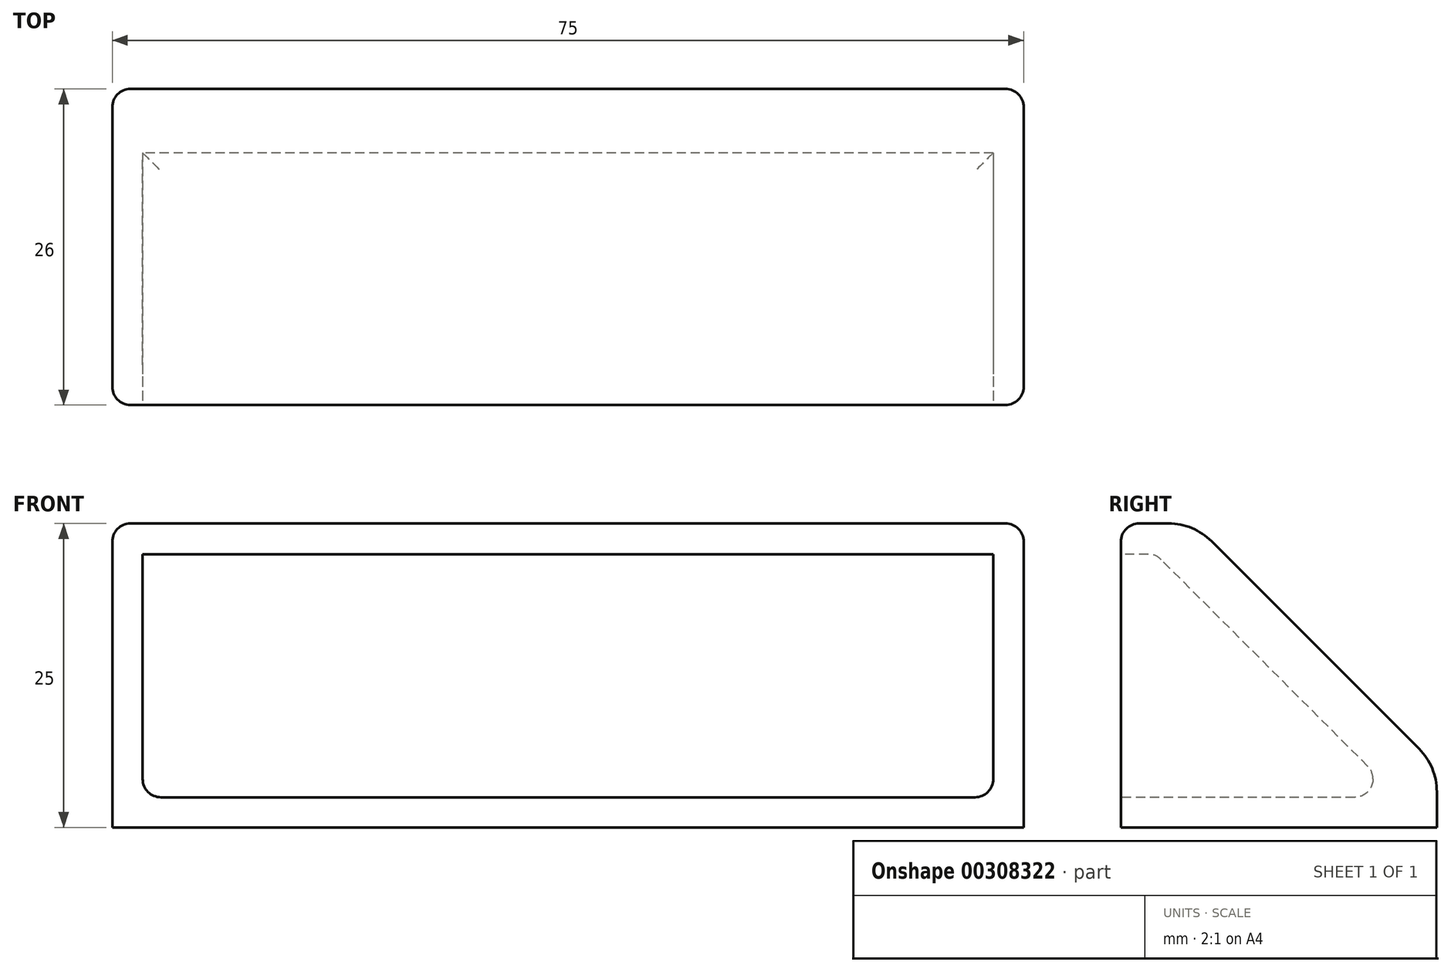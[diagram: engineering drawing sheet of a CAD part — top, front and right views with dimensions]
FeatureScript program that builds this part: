
annotation { "Feature Type Name" : "Feature", "Feature Type Description" : "" }
export const myFeature = defineFeature(function(context is Context, id is Id, definition is map)
    precondition{}
    {
        {
            var Q0;
            Q0=qCreatedBy(makeId("Top.planeOp"),FACE);
            var sketch = newSketch(context, id + "F0", { "sketchPlane" : qUnion([Q0])});
            skLineSegment(sketch, "E0.bottom", {"start": v(37.5, 13) * mm, "end": v(-37.5, 13) * mm});
            skLineSegment(sketch, "E0.top", {"start": v(37.5, -13) * mm, "end": v(-37.5, -13) * mm});
            skLineSegment(sketch, "E0.left", {"start": v(37.5, 13) * mm, "end": v(37.5, -13) * mm});
            skLineSegment(sketch, "E0.right", {"start": v(-37.5, 13) * mm, "end": v(-37.5, -13) * mm});
            skPoint(sketch, "E0.middle", {"position": v(0, 0) * mm});
            skSolve(sketch);
        }
        {
            var Q0;
            Q0=makeQuery(id+"F0.imprint","IMPRINT",FACE,{"disambiguationData":[TD([[makeQuery(id+"F0.imprint","IMPRINT",EDGE,{"derivedFrom":sQuery(id+"F0.wireOp",EDGE,"E0.bottom")}),1.0]])]});
            extrude(context, id + "F1", {"entities" : qUnion([Q0]), "depth" : 25 * mm});
        }
        {
            var Q0;
            Q0=makeQuery(id+"F1.opExtrude","CAP_EDGE",EDGE,{"disambiguationData":[OSD([sQuery(id+"F0.wireOp",EDGE,"E0.bottom")])],"isStart":false});
            chamfer(context, id + "F2", {"entities" : qUnion([Q0]), "width" : 20 * mm, "tangentPropagation" : true});
        }
        {
            var Q0;
            Q0=makeQuery(id+"F1.opExtrude","SWEPT_FACE",FACE,{"disambiguationData":[OSD([sQuery(id+"F0.wireOp",EDGE,"E0.top")])]});
            var sketch = newSketch(context, id + "F3", { "sketchPlane" : qUnion([Q0])});
            skLineSegment(sketch, "E1.bottom", {"start": v(-35, 2.48) * mm, "end": v(35, 2.48) * mm});
            skLineSegment(sketch, "E1.top", {"start": v(-35, 22.48) * mm, "end": v(35, 22.48) * mm});
            skLineSegment(sketch, "E1.left", {"start": v(-35, 2.48) * mm, "end": v(-35, 22.48) * mm});
            skLineSegment(sketch, "E1.right", {"start": v(35, 2.48) * mm, "end": v(35, 22.48) * mm});
            skSolve(sketch);
        }
        {
            var Q0;
            Q0 = qSketchRegion(id + "F3", true);
            extrude(context, id + "F4", {"entities" : qUnion([Q0]), "operationType" : NewBodyOperationType.REMOVE, "oppositeDirection" : true, "depth" : 23 * mm});
        }
        {
            var Q0;
            Q0=makeQuery(id+"F1.opExtrude","SWEPT_FACE",FACE,{"disambiguationData":[OSD([sQuery(id+"F0.wireOp",EDGE,"E0.right")])]});
            var sketch = newSketch(context, id + "F5", { "sketchPlane" : qUnion([Q0])});
            skLineSegment(sketch, "E2", {"start": v(-10.4, 7.6) * mm, "end": v(-10.4, 1.94) * mm});
            skLineSegment(sketch, "E3", {"start": v(-10.4, 1.94) * mm, "end": v(7.25, 19.6) * mm});
            skLineSegment(sketch, "E4", {"start": v(7.25, 19.6) * mm, "end": v(11.27, 23.61) * mm});
            skLineSegment(sketch, "E5", {"start": v(5.61, 23.61) * mm, "end": v(11.27, 23.61) * mm});
            skLineSegment(sketch, "E6", {"start": v(5.61, 23.61) * mm, "end": v(-10.4, 7.6) * mm});
            skSolve(sketch);
        }
        {
            var Q0;
            Q0 = qSketchRegion(id + "F5", true);
            var Q1;
            {var subQ0=sQuery(id+"F5.wireOp",EDGE,"khBEoFIl-ztzK-T5dB-HSFU-Ecbhnp3rjpfp");Q1=makeQuery(id+"F5.imprint","IMPRINT",FACE,{"disambiguationData":[TD([[makeQuery(id+"F5.imprint","IMPRINT",EDGE,{"derivedFrom":subQ0}),1.0]])]});}
            extrude(context, id + "F6", {"entities" : qUnion([Q0, Q1]), "operationType" : NewBodyOperationType.ADD, "oppositeDirection" : true, "depth" : 72.5 * mm});
        }
        {
            var Q0;
            Q0=makeQuery(id+"F1.opExtrude","SWEPT_EDGE",EDGE,{"disambiguationData":[OSD([sQuery(id+"F0.wireOp",EDGE,"E0.top"),sQuery(id+"F0.wireOp",EDGE,"E0.left")])]});
            var Q1;
            Q1=makeQuery(id+"F1.opExtrude","CAP_EDGE",EDGE,{"disambiguationData":[OSD([sQuery(id+"F0.wireOp",EDGE,"E0.top")])],"isStart":false});
            var Q2;
            Q2=makeQuery(id+"F4.boolean.opBoolean","COPY",EDGE,{"derivedFrom":makeQuery(id+"F4.opExtrude","CAP_EDGE",EDGE,{"disambiguationData":[OSD([sQuery(id+"F3.wireOp",EDGE,"E1.bottom")])],"isStart":true})});
            var Q3;
            Q3=makeQuery(id+"F4.boolean.opBoolean","COPY",EDGE,{"derivedFrom":makeQuery(id+"F4.opExtrude","CAP_EDGE",EDGE,{"disambiguationData":[OSD([sQuery(id+"F3.wireOp",EDGE,"E1.right")])],"isStart":true})});
            var Q4;
            Q4=makeQuery(id+"F4.boolean.opBoolean","COPY",EDGE,{"derivedFrom":makeQuery(id+"F4.opExtrude","CAP_EDGE",EDGE,{"disambiguationData":[OSD([sQuery(id+"F3.wireOp",EDGE,"E1.left")])],"isStart":true})});
            var Q5;
            Q5=makeQuery(id+"F4.boolean.opBoolean","COPY",EDGE,{"derivedFrom":makeQuery(id+"F4.opExtrude","CAP_EDGE",EDGE,{"disambiguationData":[OSD([sQuery(id+"F3.wireOp",EDGE,"E1.top")])],"isStart":true})});
            var Q6;
            Q6=makeQuery(id+"F1.opExtrude","SWEPT_EDGE",EDGE,{"disambiguationData":[OSD([sQuery(id+"F0.wireOp",EDGE,"E0.top"),sQuery(id+"F0.wireOp",EDGE,"E0.right")])]});
            var Q7;
            Q7=makeQuery(id+"F1.opExtrude","SWEPT_EDGE",EDGE,{"disambiguationData":[OSD([sQuery(id+"F0.wireOp",EDGE,"E0.bottom"),sQuery(id+"F0.wireOp",EDGE,"E0.left")])]});
            var Q8;
            Q8=makeQuery(id+"F2.opChamfer","BLEND_EDGE",EDGE,{"blendedFrom":[makeQuery(id+"F1.opExtrude","CAP_EDGE",EDGE,{"disambiguationData":[OSD([sQuery(id+"F0.wireOp",EDGE,"E0.bottom")])],"isStart":false}),makeQuery(id+"F1.opExtrude","SWEPT_FACE",FACE,{"disambiguationData":[OSD([sQuery(id+"F0.wireOp",EDGE,"E0.left")])]})],"blendedInto":[makeQuery(id+"F1.opExtrude","SWEPT_FACE",FACE,{"disambiguationData":[OSD([sQuery(id+"F0.wireOp",EDGE,"E0.left")])]})]});
            var Q9;
            Q9=makeQuery(id+"F1.opExtrude","CAP_EDGE",EDGE,{"disambiguationData":[OSD([sQuery(id+"F0.wireOp",EDGE,"E0.left")])],"isStart":false});
            var Q10;
            Q10=makeQuery(id+"F1.opExtrude","CAP_EDGE",EDGE,{"disambiguationData":[OSD([sQuery(id+"F0.wireOp",EDGE,"E0.right")])],"isStart":false});
            var Q11;
            Q11=makeQuery(id+"F2.opChamfer","BLEND_EDGE",EDGE,{"blendedFrom":[makeQuery(id+"F1.opExtrude","CAP_EDGE",EDGE,{"disambiguationData":[OSD([sQuery(id+"F0.wireOp",EDGE,"E0.bottom")])],"isStart":false}),makeQuery(id+"F1.opExtrude","SWEPT_FACE",FACE,{"disambiguationData":[OSD([sQuery(id+"F0.wireOp",EDGE,"E0.right")])]})],"blendedInto":[makeQuery(id+"F1.opExtrude","SWEPT_FACE",FACE,{"disambiguationData":[OSD([sQuery(id+"F0.wireOp",EDGE,"E0.right")])]})]});
            var Q12;
            Q12=makeQuery(id+"F1.opExtrude","SWEPT_EDGE",EDGE,{"disambiguationData":[OSD([sQuery(id+"F0.wireOp",EDGE,"E0.bottom"),sQuery(id+"F0.wireOp",EDGE,"E0.right")])]});
            var Q13;
            Q13=makeQuery(id+"F4.boolean.opBoolean","COPY",EDGE,{"derivedFrom":makeQuery(id+"F4.opExtrude","SWEPT_EDGE",EDGE,{"disambiguationData":[OSD([sQuery(id+"F3.wireOp",EDGE,"E1.bottom"),sQuery(id+"F3.wireOp",EDGE,"E1.left")])]})});
            var Q14;
            Q14=makeQuery(id+"F4.boolean.opBoolean","COPY",EDGE,{"derivedFrom":makeQuery(id+"F4.opExtrude","SWEPT_EDGE",EDGE,{"disambiguationData":[OSD([sQuery(id+"F3.wireOp",EDGE,"E1.bottom"),sQuery(id+"F3.wireOp",EDGE,"E1.right")])]})});
            var Q15;
            Q15=makeQuery(id+"F6.boolean.opBoolean","INTERSECT",EDGE,{"derivedFrom":[makeQuery(id+"F4.boolean.opBoolean","COPY",FACE,{"derivedFrom":makeQuery(id+"F4.opExtrude","SWEPT_FACE",FACE,{"disambiguationData":[OSD([sQuery(id+"F3.wireOp",EDGE,"E1.bottom")])]})}),makeQuery(id+"F6.opExtrude","SWEPT_FACE",FACE,{"disambiguationData":[OSD([sQuery(id+"F5.wireOp",EDGE,"E3"),sQuery(id+"F5.wireOp",EDGE,"E4")])]})]});
            var Q16;
            Q16=makeQuery(id+"F6.boolean.opBoolean","INTERSECT",EDGE,{"derivedFrom":[makeQuery(id+"F4.boolean.opBoolean","COPY",FACE,{"derivedFrom":makeQuery(id+"F4.opExtrude","SWEPT_FACE",FACE,{"disambiguationData":[OSD([sQuery(id+"F3.wireOp",EDGE,"E1.top")])]})}),makeQuery(id+"F6.opExtrude","SWEPT_FACE",FACE,{"disambiguationData":[OSD([sQuery(id+"F5.wireOp",EDGE,"E3"),sQuery(id+"F5.wireOp",EDGE,"E4")])]})]});
            fillet(context, id + "F7", {"entities" : qUnion([Q0, Q1, Q2, Q3, Q4, Q5, Q6, Q7, Q8, Q9, Q10, Q11, Q12, Q13, Q14, Q15, Q16]), "radius" : 1.5 * mm, "tangentPropagation" : true, "allowEdgeOverflow" : false});
        }
        {
            var Q0;
            {var subQ0=sQuery(id+"F0.wireOp",EDGE,"E0.bottom");Q0=makeQuery(id+"F2.opChamfer","BLEND_EDGE",EDGE,{"blendedFrom":[makeQuery(id+"F1.opExtrude","CAP_EDGE",EDGE,{"disambiguationData":[OSD([subQ0])],"isStart":false}),makeQuery(id+"F1.opExtrude","SWEPT_FACE",FACE,{"disambiguationData":[OSD([subQ0])]})],"blendedInto":[makeQuery(id+"F1.opExtrude","SWEPT_FACE",FACE,{"disambiguationData":[OSD([subQ0])]})]});}
            var Q1;
            {var subQ0=sQuery(id+"F0.wireOp",EDGE,"E0.bottom");Q1=makeQuery(id+"F2.opChamfer","BLEND_EDGE",EDGE,{"blendedFrom":[makeQuery(id+"F1.opExtrude","CAP_EDGE",EDGE,{"disambiguationData":[OSD([subQ0])],"isStart":false}),makeQuery(id+"F1.opExtrude","CAP_FACE",FACE,{"disambiguationData":[OSD([subQ0,sQuery(id+"F0.wireOp",EDGE,"E0.top"),sQuery(id+"F0.wireOp",EDGE,"E0.left"),sQuery(id+"F0.wireOp",EDGE,"E0.right")])],"isStart":false})],"blendedInto":[makeQuery(id+"F1.opExtrude","CAP_FACE",FACE,{"disambiguationData":[OSD([subQ0,sQuery(id+"F0.wireOp",EDGE,"E0.top"),sQuery(id+"F0.wireOp",EDGE,"E0.left"),sQuery(id+"F0.wireOp",EDGE,"E0.right")])],"isStart":false})]});}
            fillet(context, id + "F8", {"entities" : qUnion([Q0, Q1]), "radius" : 5 * mm, "tangentPropagation" : true, "allowEdgeOverflow" : false});
        }
    });
